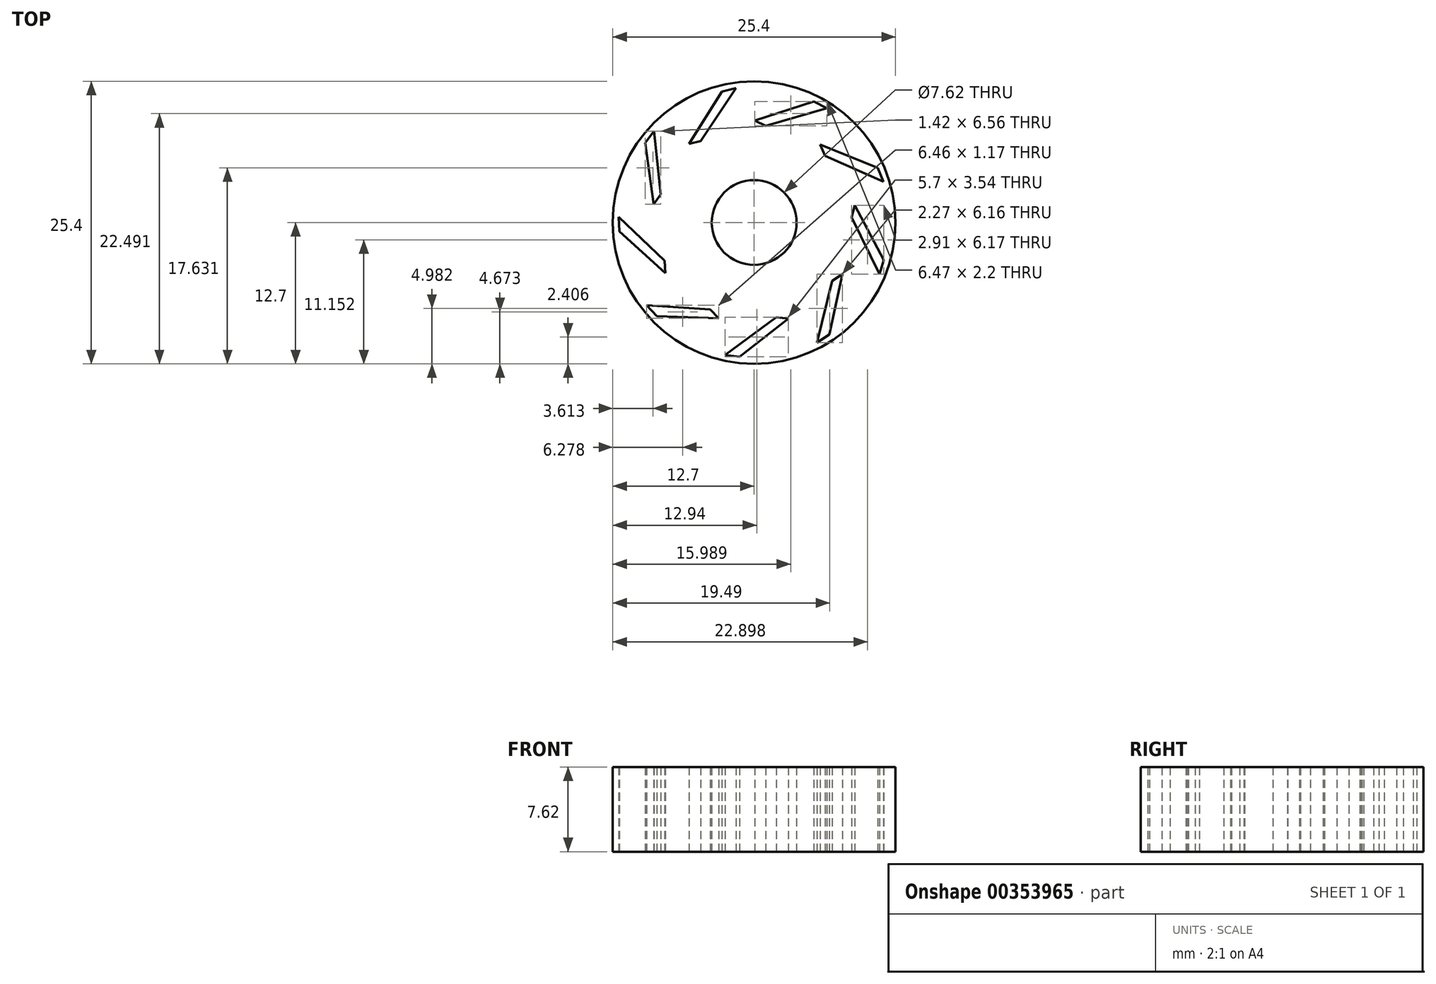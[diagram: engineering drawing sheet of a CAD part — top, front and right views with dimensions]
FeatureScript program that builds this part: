
annotation { "Feature Type Name" : "Feature", "Feature Type Description" : "" }
export const myFeature = defineFeature(function(context is Context, id is Id, definition is map)
    precondition{}
    {
        {
            var Q0;
            Q0=qCreatedBy(makeId("Top.planeOp"),FACE);
            var sketch = newSketch(context, id + "F0", { "sketchPlane" : qUnion([Q0])});
            skCircle(sketch, "E0", {"center": v(0, 0) * mm, "radius": 3.81 * mm});
            skCircle(sketch, "E1", {"center": v(0, 0) * mm, "radius": 12.7 * mm});
            skLineSegment(sketch, "E2", {"start": v(-9.8, 7.16) * mm, "end": v(-9.03, 1.65) * mm});
            skLineSegment(sketch, "E3", {"start": v(-9.03, 1.65) * mm, "end": v(-8.38, 2.54) * mm});
            skLineSegment(sketch, "E4", {"start": v(-8.38, 2.54) * mm, "end": v(-9, 8.21) * mm});
            skLineSegment(sketch, "E5", {"start": v(-9, 8.21) * mm, "end": v(-9.8, 7.16) * mm});
            skLineSegment(sketch, "E6.1.0", {"start": v(-8.05, -3.44) * mm, "end": v(-12.18, 0.5) * mm});
            skLineSegment(sketch, "E6.1.1", {"start": v(-12.18, 0.5) * mm, "end": v(-12.1, -0.81) * mm});
            skLineSegment(sketch, "E6.1.2", {"start": v(-12.1, -0.81) * mm, "end": v(-7.98, -4.54) * mm});
            skLineSegment(sketch, "E6.1.3", {"start": v(-7.98, -4.54) * mm, "end": v(-8.05, -3.44) * mm});
            skLineSegment(sketch, "E6.2.0", {"start": v(-3.96, -7.81) * mm, "end": v(-9.65, -7.44) * mm});
            skLineSegment(sketch, "E6.2.1", {"start": v(-9.65, -7.44) * mm, "end": v(-8.75, -8.4) * mm});
            skLineSegment(sketch, "E6.2.2", {"start": v(-8.75, -8.4) * mm, "end": v(-3.2, -8.6) * mm});
            skLineSegment(sketch, "E6.2.3", {"start": v(-3.2, -8.6) * mm, "end": v(-3.96, -7.81) * mm});
            skLineSegment(sketch, "E7.2.3.0", {"start": v(2, -8.53) * mm, "end": v(-2.6, -11.9) * mm});
            skLineSegment(sketch, "E7.3.3.0", {"start": v(-2.6, -11.9) * mm, "end": v(-1.3, -12.06) * mm});
            skLineSegment(sketch, "E7.6.3.0", {"start": v(-1.3, -12.06) * mm, "end": v(3.09, -8.65) * mm});
            skLineSegment(sketch, "E7.9.3.0", {"start": v(3.09, -8.65) * mm, "end": v(2, -8.53) * mm});
            skLineSegment(sketch, "E7.2.4.0", {"start": v(7, -5.25) * mm, "end": v(5.65, -10.8) * mm});
            skLineSegment(sketch, "E7.3.4.0", {"start": v(5.65, -10.8) * mm, "end": v(6.76, -10.08) * mm});
            skLineSegment(sketch, "E7.6.4.0", {"start": v(6.76, -10.08) * mm, "end": v(7.92, -4.64) * mm});
            skLineSegment(sketch, "E7.9.4.0", {"start": v(7.92, -4.64) * mm, "end": v(7, -5.25) * mm});
            skLineSegment(sketch, "E8.2.5.0", {"start": v(8.74, 0.48) * mm, "end": v(11.27, -4.64) * mm});
            skLineSegment(sketch, "E8.3.5.0", {"start": v(11.27, -4.64) * mm, "end": v(11.65, -3.38) * mm});
            skLineSegment(sketch, "E8.6.5.0", {"start": v(11.65, -3.38) * mm, "end": v(9.05, 1.54) * mm});
            skLineSegment(sketch, "E8.9.5.0", {"start": v(9.05, 1.54) * mm, "end": v(8.74, 0.48) * mm});
            skLineSegment(sketch, "E9.2.6.0", {"start": v(6.39, 5.99) * mm, "end": v(11.61, 3.7) * mm});
            skLineSegment(sketch, "E9.3.6.0", {"start": v(11.61, 3.7) * mm, "end": v(11.1, 4.9) * mm});
            skLineSegment(sketch, "E9.6.6.0", {"start": v(11.1, 4.9) * mm, "end": v(5.95, 7) * mm});
            skLineSegment(sketch, "E9.9.6.0", {"start": v(5.95, 7) * mm, "end": v(6.39, 5.99) * mm});
            skLineSegment(sketch, "E10.2.7.0", {"start": v(1.05, 8.7) * mm, "end": v(6.52, 10.3) * mm});
            skLineSegment(sketch, "E10.3.7.0", {"start": v(6.52, 10.3) * mm, "end": v(5.35, 10.89) * mm});
            skLineSegment(sketch, "E10.6.7.0", {"start": v(5.35, 10.89) * mm, "end": v(0.06, 9.18) * mm});
            skLineSegment(sketch, "E10.9.7.0", {"start": v(0.06, 9.18) * mm, "end": v(1.05, 8.7) * mm});
            skLineSegment(sketch, "E11.2.8.0", {"start": v(-4.79, 7.33) * mm, "end": v(-1.62, 12.08) * mm});
            skLineSegment(sketch, "E11.3.8.0", {"start": v(-1.62, 12.08) * mm, "end": v(-2.9, 11.78) * mm});
            skLineSegment(sketch, "E11.6.8.0", {"start": v(-2.9, 11.78) * mm, "end": v(-5.86, 7.07) * mm});
            skLineSegment(sketch, "E11.9.8.0", {"start": v(-5.86, 7.07) * mm, "end": v(-4.79, 7.33) * mm});
            skSolve(sketch);
        }
        {
            var Q0;
            Q0 = qSketchRegion(id + "F0", true);
            extrude(context, id + "F1", {"entities" : qUnion([Q0]), "endBound" : BoundingType.SYMMETRIC, "depth" : 7.62 * mm});
        }
    });
